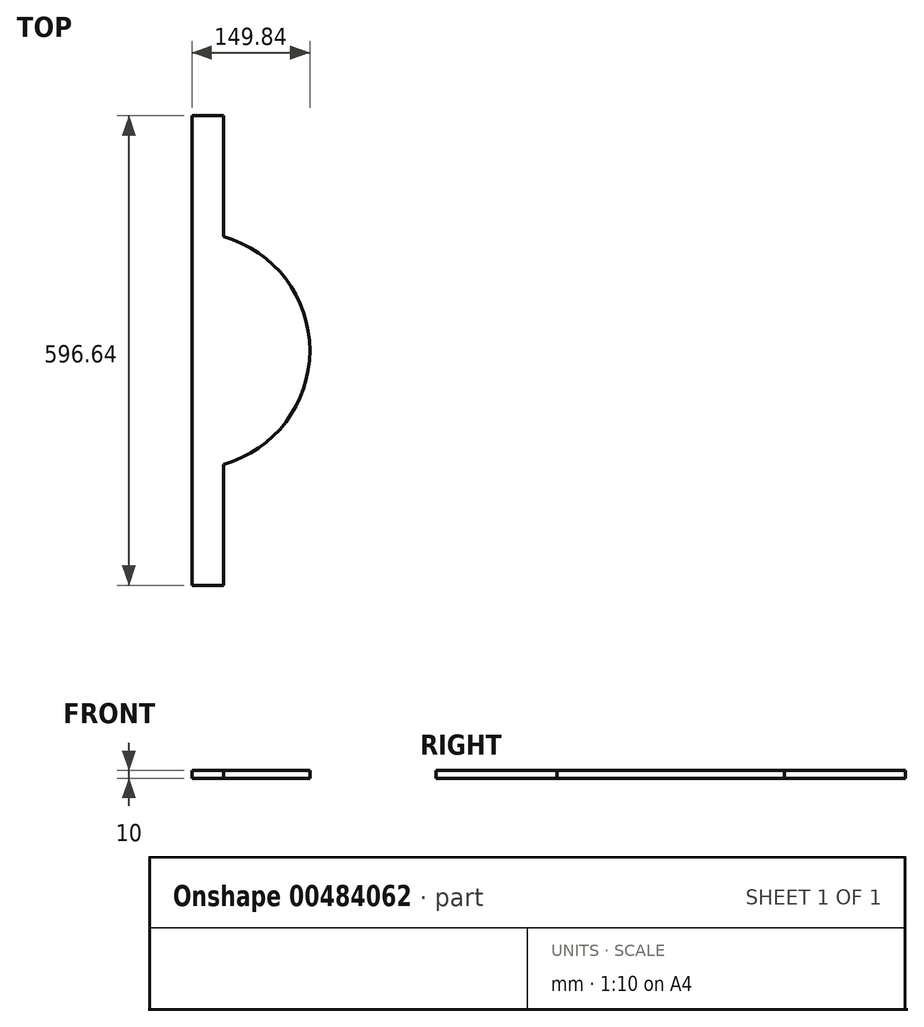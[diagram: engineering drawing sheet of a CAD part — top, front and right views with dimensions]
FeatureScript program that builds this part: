
annotation { "Feature Type Name" : "Feature", "Feature Type Description" : "" }
export const myFeature = defineFeature(function(context is Context, id is Id, definition is map)
    precondition{}
    {
        {
            var Q0;
            Q0=qCreatedBy(makeId("Top.planeOp"),FACE);
            var sketch = newSketch(context, id + "F0", { "sketchPlane" : qUnion([Q0])});
            skLineSegment(sketch, "E0", {"start": v(40, -298.32) * mm, "end": v(45, -298.32) * mm});
            skLineSegment(sketch, "E1", {"start": v(40, 144.57) * mm, "end": v(40, 298.32) * mm});
            skArc(sketch, "E2", {"start": v(43.54, -143.54) * mm, "mid": v(149.89, 1.85) * mm, "end": v(40, 144.57) * mm});
            skLineSegment(sketch, "E3", {"start": v(40, -148.32) * mm, "end": v(40, -298.32) * mm});
            skPoint(sketch, "E4.visualSharp", {"position": v(45, 148.32) * mm});
            skPoint(sketch, "E5.visualSharp", {"position": v(40, -144.57) * mm});
            skLineSegment(sketch, "E6", {"start": v(40, 298.32) * mm, "end": v(0, 298.32) * mm});
            skLineSegment(sketch, "E7", {"start": v(0, 298.32) * mm, "end": v(0, -298.32) * mm});
            skLineSegment(sketch, "E8", {"start": v(0, -298.32) * mm, "end": v(40, -298.32) * mm});
            skLineSegment(sketch, "E9", {"start": v(40, -298.32) * mm, "end": v(40, -144.57) * mm});
            skLineSegment(sketch, "E10", {"start": v(40, 298.32) * mm, "end": v(40, 144.57) * mm});
            skArc(sketch, "E11", {"start": v(40, -144.57) * mm, "mid": v(149.84, 0) * mm, "end": v(40, 144.57) * mm});
            skSolve(sketch);
        }
        {
            var Q0;
            Q0 = qSketchRegion(id + "F0", true);
            extrude(context, id + "F1", {"entities" : qUnion([Q0]), "depth" : 10 * mm, "offsetDistance" : 25 * mm});
        }
    });
